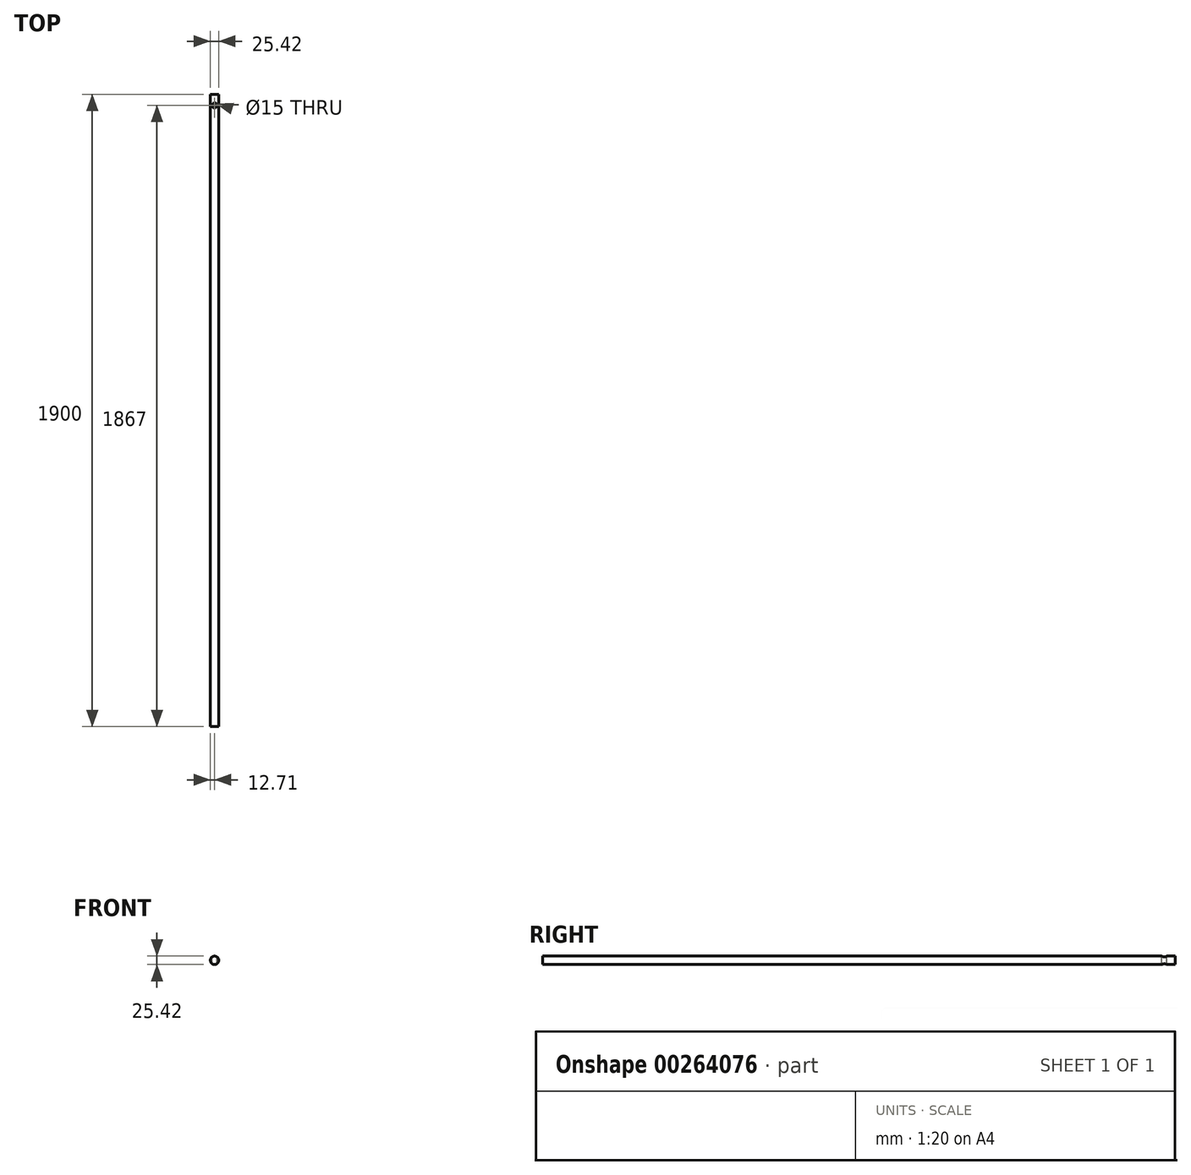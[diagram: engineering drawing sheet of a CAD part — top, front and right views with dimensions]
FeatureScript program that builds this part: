
annotation { "Feature Type Name" : "Feature", "Feature Type Description" : "" }
export const myFeature = defineFeature(function(context is Context, id is Id, definition is map)
    precondition{}
    {
        {
            assignVariable(context, id + "F0", {"name" : "diametro", "anyValue" : 2 * 12.7});
        }
        {
            var Q0;
            Q0=qCreatedBy(makeId("Front.planeOp"),FACE);
            var sketch = newSketch(context, id + "F1", { "sketchPlane" : qUnion([Q0])});
            skCircle(sketch, "E0", {"center": v(0, 0) * mm, "radius": 12.7 * mm});
            skSolve(sketch);
        }
        {
            var Q0;
            Q0=qCreatedBy(makeId("Top.planeOp"),FACE);
            var sketch = newSketch(context, id + "F2", { "sketchPlane" : qUnion([Q0])});
            skLineSegment(sketch, "E1", {"start": v(0, 0) * mm, "end": v(0, -33) * mm});
            skLineSegment(sketch, "E2", {"start": v(0, 0) * mm, "end": v(0, -45) * mm});
            skCircle(sketch, "E3", {"center": v(0, -33) * mm, "radius": 7.5 * mm});
            skSolve(sketch);
        }
        {
            var Q0;
            Q0=makeQuery(id+"F1.imprint","IMPRINT",FACE,{"disambiguationData":[TD([[makeQuery(id+"F1.imprint","IMPRINT",EDGE,{"derivedFrom":sQuery(id+"F1.wireOp",EDGE,"E0")}),1.0]])]});
            extrude(context, id + "F3", {"entities" : qUnion([Q0]), "depth" : 1900 * mm});
        }
        {
            var Q0;
            {var subQ0=sQuery(id+"F2.wireOp",EDGE,"E2");var subQ1=makeQuery(id+"F2.imprint","IMPRINT",VERTEX,{"derivedFrom":subQ0});Q0=makeQuery(id+"F2.imprint","IMPRINT",FACE,{"disambiguationData":[TD([[makeQuery(id+"F2.imprint","IMPRINT",EDGE,{"disambiguationData":[TD([[subQ1,1.0]])],"derivedFrom":subQ0}),-1.0]])]});}
            var Q1;
            {var subQ0=sQuery(id+"F2.wireOp",EDGE,"E2");var subQ1=makeQuery(id+"F2.imprint","IMPRINT",VERTEX,{"derivedFrom":subQ0});Q1=makeQuery(id+"F2.imprint","IMPRINT",FACE,{"disambiguationData":[TD([[makeQuery(id+"F2.imprint","IMPRINT",EDGE,{"disambiguationData":[TD([[subQ1,1.0]])],"derivedFrom":subQ0}),1.0]])]});}
            extrude(context, id + "F4", {"entities" : qUnion([Q0, Q1]), "operationType" : NewBodyOperationType.REMOVE, "oppositeDirection" : true, "depth" : 0.5 * (getVariable(context, 'diametro')) * mm, "hasSecondDirection" : true, "secondDirectionOppositeDirection" : false, "secondDirectionDepth" : 0.5 * (getVariable(context, 'diametro')) * mm});
        }
    });
